# Revit family: Electronics_Community-Point-Source_Biamp_Loudspeaker_R_2-MAX
name_source: partatom
category: Communication Devices
units: mm (PartAtom-declared; Revit-internal decimal feet)

## family parameters
Cut with Voids When Loaded = No
Host = Face
Maintain Annotation Orientation = No
OmniClass Number = 23.85.10.11.14.14.14
Part Type = Normal
Room Calculation Point = No
Round Connector Dimension = Use Diameter
Shared = No

## types (4) — shared parameters
Connector Description = Terminal strip; 1200W 8 ohms (4800W peak) 98 V
Default Elevation = 48 "
Depth = 30.75 "
Description = R2-MAX High Output Full-Range 60° x 40° Weather-Resistant Loudspeaker
Environmental = IP55 per IEC 60529, conforms with MIL-STD-810G
Finish = Refer to the Technical Drawing (page 4)
Grill Material = Biamp - Plastic - Gray(Grid)
Height = 24.76 "
Housing Material = Biamp - Plastic - Gray
Input Connection = 2 x 12' (3.6 m) 16-2 SJOW cables
Manufacturer = Biamp
Mounting Points = (5) 1/2-13 threaded rigging points, Steel zinc-rich epoxy dual-layer powder-coated bracket with (2) aluminum aiming straps to secure angle
Operating Environment = Indoor /  Continuous outdoor direct exposure
Operating Mode = Biamp with DSP (Passive MF/HF)
Product Documentation Link = https://downloads.biamp.com
Product Page URL = https://www.biamp.com
Product data url = https://www.bimobject.com
Recommended Amplifers = LF - 1200W - 2400W @ 8 ohms,  (98V - 139V); MF/HF - 350W - 700W @ 8 ohms,  (53V - 75V)
URL = https://www.biamp.com
Width = 24.76 "
Yoke Material = Biamp - Metal - Gray

## per-type parameters (varying)
| type | Equalized Maximum SPL | Equalized Sensitivity | Nominal Beamwidth  (H x V) | Nominal Maximum SPL (Whole Space) | Nominal Sensitivity | Operating Range | Transducers | Weight |
| R2-52MAX | Peak - 141dB; Continuous - 135dB | 1W - 104dB; 2.83V - 104dB | 50° x  20° | Peak - LF - 139dB,MF/HF - 141dB; Continuous - LF - 133dB,MF/HF - 135dB | 1W - LF - 103dB,MF/HF - 110dB; 2.83V - LF - 102dB,MF/HF - 110dB | 71 Hz to 19.5 kHz | LF –2 x 12 inherently weather-resistant cones with 3 voice coil,neodymium motor and aluminum demodulation ring MF - 2 x 2 exit, M200HP compression, 3.5 diaphragm, 2.2 Voice coil, high temp non-metallic diaphragm  HF – 1 x 1 exit compression, 1.7 voice coil, demodulation ring, ketone polymer diaphragm | 55.30 kgf |
| R2-64MAX | Peak - 139dB; Continuous - 133dB | 1W - 102dB; 2.83V - 102dB | 60° x  40° | Peak - LF - 140dB,MF/HF - 140dB; Continuous - LF - 134dB,MF/HF - 134dB | 1W - LF - 103dB,MF/HF - 109dB; 2.83V - LF - 103dB,MF/HF - 109dB | 71 Hz to 22.4 kHz | LF –2 x 12 inherently weather-resistant cones with 3 voice coil, neodymium motor and aluminum demodulation ring MF - 1 x 2 exit, M200HP compression, 3.5 diaphragm, 2.2 Voice coil,high temp non-metallic diaphragm  HF – 1 x 1.4 exit compression, 2.87 voice coil, copper shorting ring, titanium diaphragm with mylar surround | 52.20 kgf |
| R2-94MAX | Peak - 140dB; Continuous - 134dB | 1W - 103dB; 2.83V - 103dB | 90° x  40° | Peak - LF - 140dB,MF/HF - 137dB; Continuous - LF - 134dB,MF/HF - 131dB | 1W - LF - 103dB,MF/HF - 106dB; 2.83V - LF - 103dB,MF/HF - 106dB | 73 Hz to 22.4 kHz | LF –2 x 12 inherently weather-resistant cones with 3 voice coil,neodymium motor and aluminum demodulation ring MF - 1 x 2 exit, M200HP compression, 3.5 diaphragm, 2.2 Voice coil,high temp non-metallic diaphragm HF – 1 x 1.4 exit compression, 2.87 voice coil, copper shorting ring,titanium diaphragm with mylar surround | 52.20 kgf |
| R2-66MAX | Peak - 140dB; Continuous - 134dB | 1W - 103dB; 2.83V - 103dB | 60° x  60° | Peak - LF - 140dB,MF/HF - 139dB; Continuous - LF - 134dB,MF/HF - 133dB | 1W - LF - 103dB,MF/HF - 108dB; 2.83V - LF - 103dB,MF/HF - 108dB | 73 Hz to 22.4 kHz | LF –2 x 12 inherently weather-resistant cones with 3 voice coil,neodymium motor and aluminum demodulation ring MF - 1 x 2 exit, M200HP compression, 3.5 diaphragm, 2.2 Voice coil,high temp non-metallic diaphragm HF – 1 x 1.4 exit compression, 2.87 voice coil, copper shorting ring,titanium diaphragm with mylar surround | 52.20 kgf |

note: column(s) folded — value = type name in every type: Model

## geometry (parser evidence)
native form markers: Sweep x4
no freeform markers — native parametric forms only
